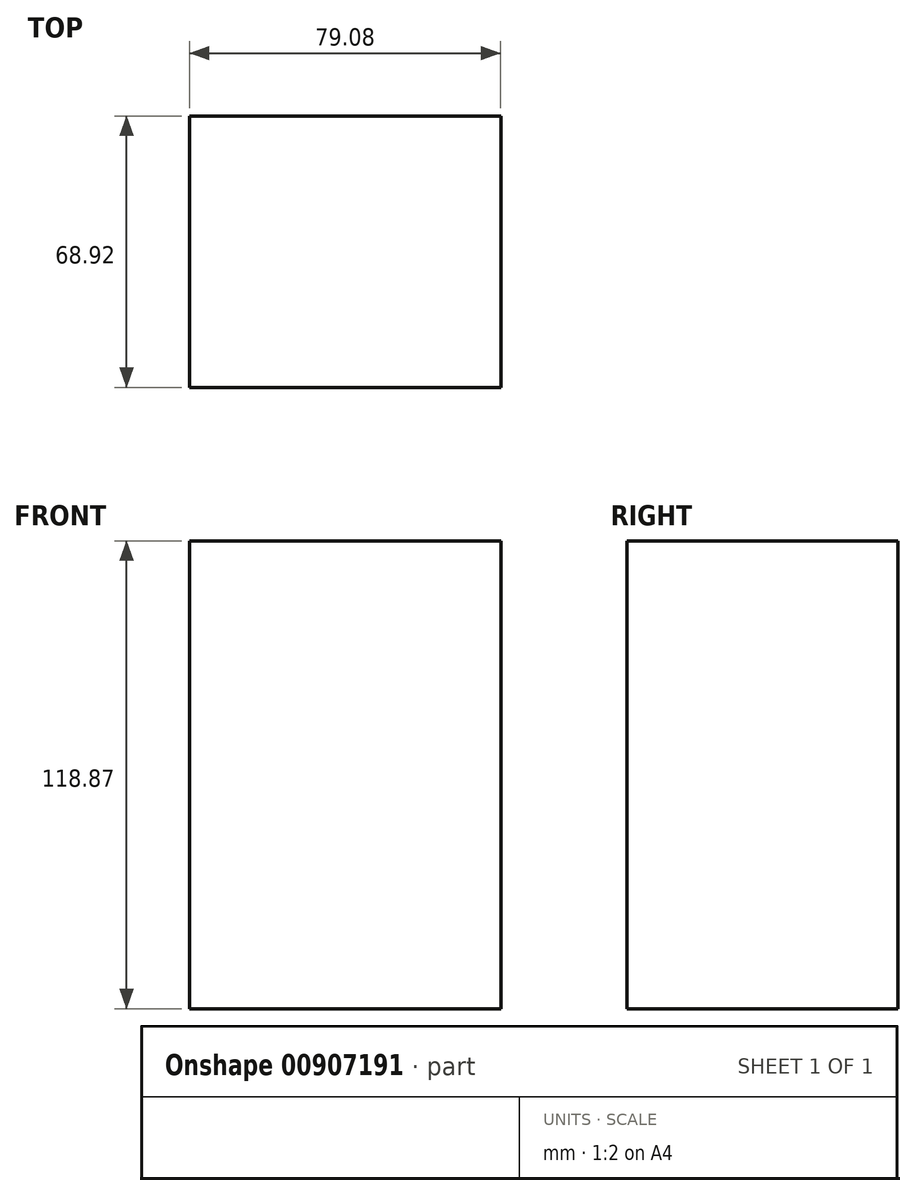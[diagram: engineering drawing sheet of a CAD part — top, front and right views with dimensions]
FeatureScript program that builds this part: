
annotation { "Feature Type Name" : "Feature", "Feature Type Description" : "" }
export const myFeature = defineFeature(function(context is Context, id is Id, definition is map)
    precondition{}
    {
        {
            var Q0;
            Q0=qCreatedBy(makeId("Top.planeOp"),FACE);
            var sketch = newSketch(context, id + "F0", { "sketchPlane" : qUnion([Q0])});
            skLineSegment(sketch, "E0.bottom", {"start": v(-39.47, -21.88) * mm, "end": v(39.61, -21.88) * mm});
            skLineSegment(sketch, "E0.top", {"start": v(-39.47, 47.04) * mm, "end": v(39.61, 47.04) * mm});
            skLineSegment(sketch, "E0.left", {"start": v(-39.47, -21.88) * mm, "end": v(-39.47, 47.04) * mm});
            skLineSegment(sketch, "E0.right", {"start": v(39.61, -21.88) * mm, "end": v(39.61, 47.04) * mm});
            skSolve(sketch);
        }
        {
            var Q0;
            Q0 = qSketchRegion(id + "F0", true);
            extrude(context, id + "F1", {"entities" : qUnion([Q0]), "depth" : 118.87 * mm, "offsetDistance" : 25.4 * mm});
        }
    });
